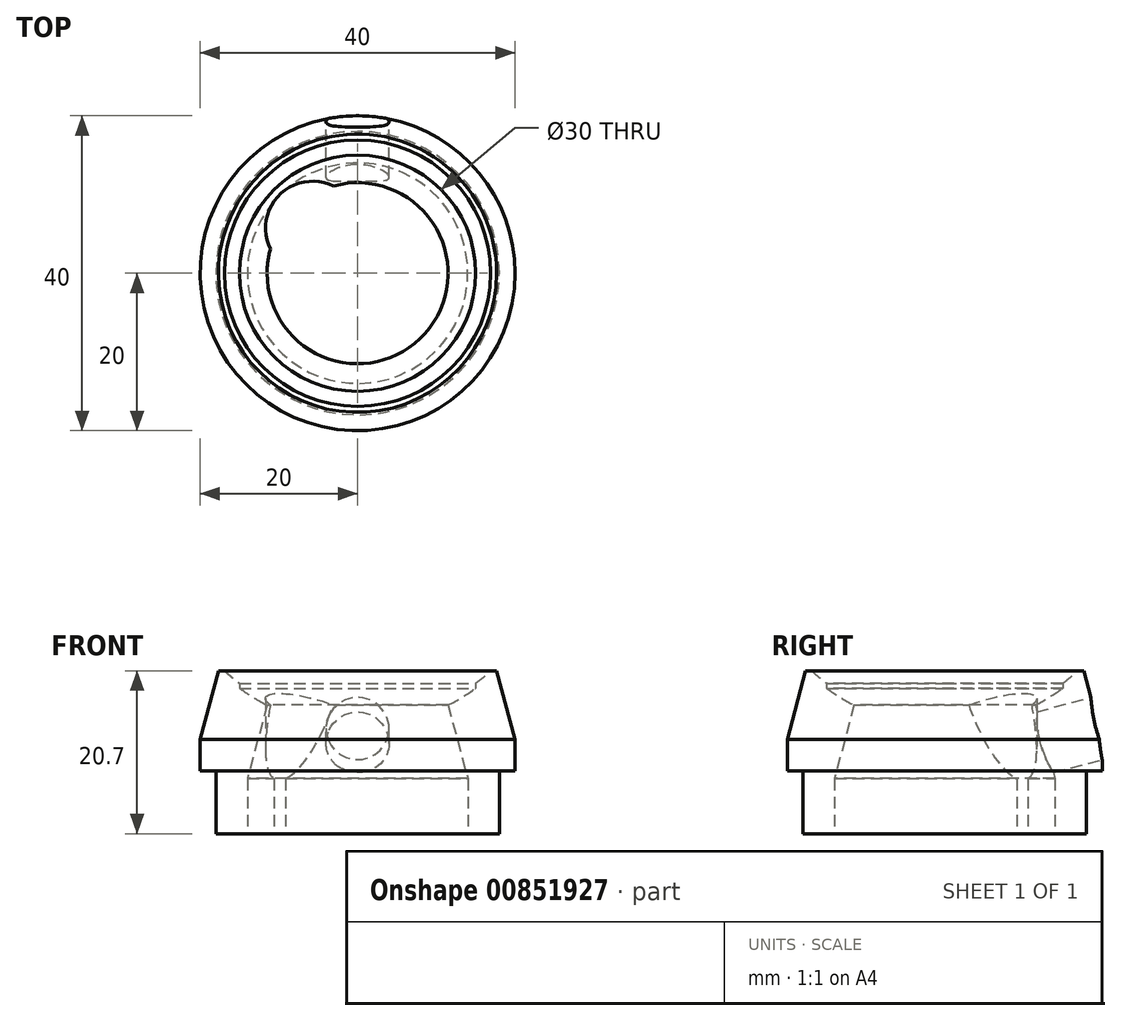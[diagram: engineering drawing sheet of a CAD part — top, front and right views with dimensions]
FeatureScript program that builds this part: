
annotation { "Feature Type Name" : "Feature", "Feature Type Description" : "" }
export const myFeature = defineFeature(function(context is Context, id is Id, definition is map)
    precondition{}
    {
        {
            var Q0;
            Q0=qCreatedBy(makeId("Right.planeOp"),FACE);
            var sketch = newSketch(context, id + "F0", { "sketchPlane" : qUnion([Q0])});
            skLineSegment(sketch, "E0", {"start": v(0, 12.7) * mm, "end": v(-17.67, 12.7) * mm});
            skLineSegment(sketch, "E1", {"start": v(-17.67, 12.7) * mm, "end": v(-20, 4) * mm});
            skLineSegment(sketch, "E2", {"start": v(-20, 4) * mm, "end": v(-20, 0) * mm});
            skLineSegment(sketch, "E3", {"start": v(-20, 0) * mm, "end": v(-18, 0) * mm});
            skLineSegment(sketch, "E4", {"start": v(-18, 0) * mm, "end": v(-18, -8) * mm});
            skLineSegment(sketch, "E5", {"start": v(-18, -8) * mm, "end": v(0, -8) * mm});
            skLineSegment(sketch, "E6", {"start": v(0, 12.7) * mm, "end": v(0, -8) * mm});
            skSolve(sketch);
        }
        {
            var Q0;
            Q0=makeQuery(id+"F0.imprint","IMPRINT",FACE,{"disambiguationData":[TD([[makeQuery(id+"F0.imprint","IMPRINT",EDGE,{"derivedFrom":sQuery(id+"F0.wireOp",EDGE,"E0")}),1.0]])]});
            var Q1;
            Q1=sQuery(id+"F0.wireOp",EDGE,"E6");
            revolve(context, id + "F1", {"surfaceOperationType" : NewSurfaceOperationType.NEW, "entities" : qUnion([Q0]), "axis" : qUnion([Q1]), "revolveType" : RevolveType.FULL});
        }
        {
            var Q0;
            Q0=qCreatedBy(makeId("Right.planeOp"),FACE);
            var sketch = newSketch(context, id + "F2", { "sketchPlane" : qUnion([Q0])});
            skArc(sketch, "E7", {"start": v(-16.92, 12.7) * mm, "mid": v(0, 6.1) * mm, "end": v(16.92, 12.7) * mm});
            skLineSegment(sketch, "E8.0", {"start": v(-17.67, 12.7) * mm, "end": v(17.67, 12.7) * mm, "construction": true});
            skLineSegment(sketch, "E9", {"start": v(0, 12.7) * mm, "end": v(0, 6.1) * mm});
            skLineSegment(sketch, "E10", {"start": v(0, 12.7) * mm, "end": v(-16.92, 12.7) * mm});
            skSolve(sketch);
        }
        {
            var Q0;
            Q0 = qSketchRegion(id + "F2", true);
            var Q1;
            Q1=sQuery(id+"F2.wireOp",EDGE,"E9");
            revolve(context, id + "F3", {"operationType" : NewBodyOperationType.REMOVE, "surfaceOperationType" : NewSurfaceOperationType.NEW, "entities" : qUnion([Q0]), "axis" : qUnion([Q1]), "revolveType" : RevolveType.FULL, "oppositeDirection" : true});
        }
        {
            var Q0;
            Q0=qCreatedBy(makeId("Right.planeOp"),FACE);
            var sketch = newSketch(context, id + "F4", { "sketchPlane" : qUnion([Q0])});
            skArc(sketch, "E11", {"start": v(-15.82, 11.1) * mm, "mid": v(-8.37, 7.02) * mm, "end": v(0, 5.6) * mm});
            skLineSegment(sketch, "E12", {"start": v(-15.82, 11.1) * mm, "end": v(0, 11.1) * mm});
            skLineSegment(sketch, "E13", {"start": v(0, 11.1) * mm, "end": v(0, 5.6) * mm});
            skArc(sketch, "E14", {"start": v(-16.92, 12.7) * mm, "mid": v(0, 6.1) * mm, "end": v(16.92, 12.7) * mm, "construction": true});
            skLineSegment(sketch, "E15", {"start": v(-15, 11.1) * mm, "end": v(-15, 10.48) * mm});
            skSolve(sketch);
        }
        {
            var Q0;
            {var subQ0=sQuery(id+"F4.wireOp",EDGE,"E13");Q0=makeQuery(id+"F4.imprint","IMPRINT",FACE,{"disambiguationData":[TD([[makeQuery(id+"F4.imprint","IMPRINT",EDGE,{"derivedFrom":subQ0}),-1.0]])]});}
            var Q1;
            Q1=sQuery(id+"F4.wireOp",EDGE,"E13");
            revolve(context, id + "F5", {"operationType" : NewBodyOperationType.REMOVE, "surfaceOperationType" : NewSurfaceOperationType.NEW, "entities" : qUnion([Q0]), "axis" : qUnion([Q1]), "revolveType" : RevolveType.FULL, "oppositeDirection" : true});
        }
        {
            var Q0;
            Q0=makeQuery(id+"F1.opRevolve","SWEPT_FACE",FACE,{"disambiguationData":[OSD([sQuery(id+"F0.wireOp",EDGE,"E5")])]});
            var sketch = newSketch(context, id + "F6", { "sketchPlane" : qUnion([Q0])});
            skCircle(sketch, "E16", {"center": v(0, 0) * mm, "radius": 14 * mm});
            skSolve(sketch);
        }
        {
            var Q0;
            Q0=makeQuery(id+"F6.imprint","IMPRINT",FACE,{"disambiguationData":[TD([[makeQuery(id+"F6.imprint","IMPRINT",EDGE,{"derivedFrom":sQuery(id+"F6.wireOp",EDGE,"E16")}),1.0]])]});
            extrude(context, id + "F7", {"entities" : qUnion([Q0]), "operationType" : NewBodyOperationType.REMOVE, "oppositeDirection" : true, "depth" : 7 * mm, "offsetDistance" : 25 * mm});
        }
        {
            var Q0;
            Q0=qCreatedBy(makeId("Right.planeOp"),FACE);
            var sketch = newSketch(context, id + "F8", { "sketchPlane" : qUnion([Q0])});
            skArc(sketch, "E17", {"start": v(-15, 10.48) * mm, "mid": v(0, 5.6) * mm, "end": v(15, 10.48) * mm, "construction": true});
            skLineSegment(sketch, "E18", {"start": v(-14, -8) * mm, "end": v(-14, -1) * mm, "construction": true});
            skLineSegment(sketch, "E19", {"start": v(14, -1) * mm, "end": v(14, -8) * mm, "construction": true});
            skLineSegment(sketch, "E20", {"start": v(-14, -1) * mm, "end": v(-11.5, 8.34) * mm});
            skLineSegment(sketch, "E21", {"start": v(-11.5, 8.34) * mm, "end": v(0, 8.34) * mm});
            skLineSegment(sketch, "E22", {"start": v(0, 8.34) * mm, "end": v(0, -1) * mm});
            skLineSegment(sketch, "E23", {"start": v(0, -1) * mm, "end": v(-14, -1) * mm});
            skSolve(sketch);
        }
        {
            var Q0;
            Q0=makeQuery(id+"F8.imprint","IMPRINT",FACE,{"disambiguationData":[TD([[makeQuery(id+"F8.imprint","IMPRINT",EDGE,{"derivedFrom":sQuery(id+"F8.wireOp",EDGE,"E20")}),-1.0]])]});
            var Q1;
            Q1=sQuery(id+"F8.wireOp",EDGE,"E22");
            revolve(context, id + "F9", {"operationType" : NewBodyOperationType.REMOVE, "surfaceOperationType" : NewSurfaceOperationType.NEW, "entities" : qUnion([Q0]), "axis" : qUnion([Q1]), "revolveType" : RevolveType.FULL, "oppositeDirection" : true});
        }
        {
            var Q0;
            Q0=qCreatedBy(makeId("Top.planeOp"),FACE);
            var sketch = newSketch(context, id + "F10", { "sketchPlane" : qUnion([Q0])});
            skCircle(sketch, "E24", {"center": v(-5.7, 5.7) * mm, "radius": 6 * mm});
            skLineSegment(sketch, "E25", {"start": v(-5.7, 5.7) * mm, "end": v(0, 0) * mm});
            skSolve(sketch);
        }
        {
            var Q0;
            Q0=makeQuery(id+"F10.imprint","IMPRINT",FACE,{"disambiguationData":[TD([[makeQuery(id+"F10.imprint","IMPRINT",EDGE,{"derivedFrom":sQuery(id+"F10.wireOp",EDGE,"E24")}),1.0]])]});
            extrude(context, id + "F11", {"entities" : qUnion([Q0]), "operationType" : NewBodyOperationType.REMOVE, "endBound" : BoundingType.THROUGH_ALL, "depth" : 25 * mm, "offsetDistance" : 25 * mm, "hasSecondDirection" : true, "secondDirectionBound" : BoundingType.THROUGH_ALL, "secondDirectionOppositeDirection" : true, "secondDirectionDepth" : 25 * mm});
        }
        {
            var Q0;
            Q0=qCreatedBy(makeId("Right.planeOp"),FACE);
            var sketch = newSketch(context, id + "F12", { "sketchPlane" : qUnion([Q0])});
            skLineSegment(sketch, "E26", {"start": v(17.67, 12.7) * mm, "end": v(20, 4) * mm});
            skLineSegment(sketch, "E27", {"start": v(18.83, 8.35) * mm, "end": v(9.18, 5.76) * mm});
            skSolve(sketch);
        }
        {
            var Q0;
            Q0=sQuery(id+"F12.wireOp",EDGE,"E27");
            var Q1;
            Q1=sQuery(id+"F12.wireOp",VERTEX,"E27.start");
            cPlane(context, id + "F13", {"entities" : qUnion([Q0, Q1]), "cplaneType" : CPlaneType.LINE_POINT, "offset" : 25 * mm, "width" : 150 * mm, "height" : 150 * mm});
        }
        {
            var Q0;
            Q0=qCreatedBy(id+"F13.planeOp",FACE);
            var sketch = newSketch(context, id + "F14", { "sketchPlane" : qUnion([Q0])});
            skCircle(sketch, "E28", {"center": v(0, 0.2) * mm, "radius": 4 * mm});
            skSolve(sketch);
        }
        {
            var Q0;
            Q0=makeQuery(id+"F14.imprint","IMPRINT",FACE,{"disambiguationData":[TD([[makeQuery(id+"F14.imprint","IMPRINT",EDGE,{"derivedFrom":sQuery(id+"F14.wireOp",EDGE,"E28")}),1.0]])]});
            extrude(context, id + "F15", {"entities" : qUnion([Q0]), "operationType" : NewBodyOperationType.REMOVE, "endBound" : BoundingType.UP_TO_NEXT, "depth" : 25 * mm, "offsetDistance" : 25 * mm});
        }
    });
